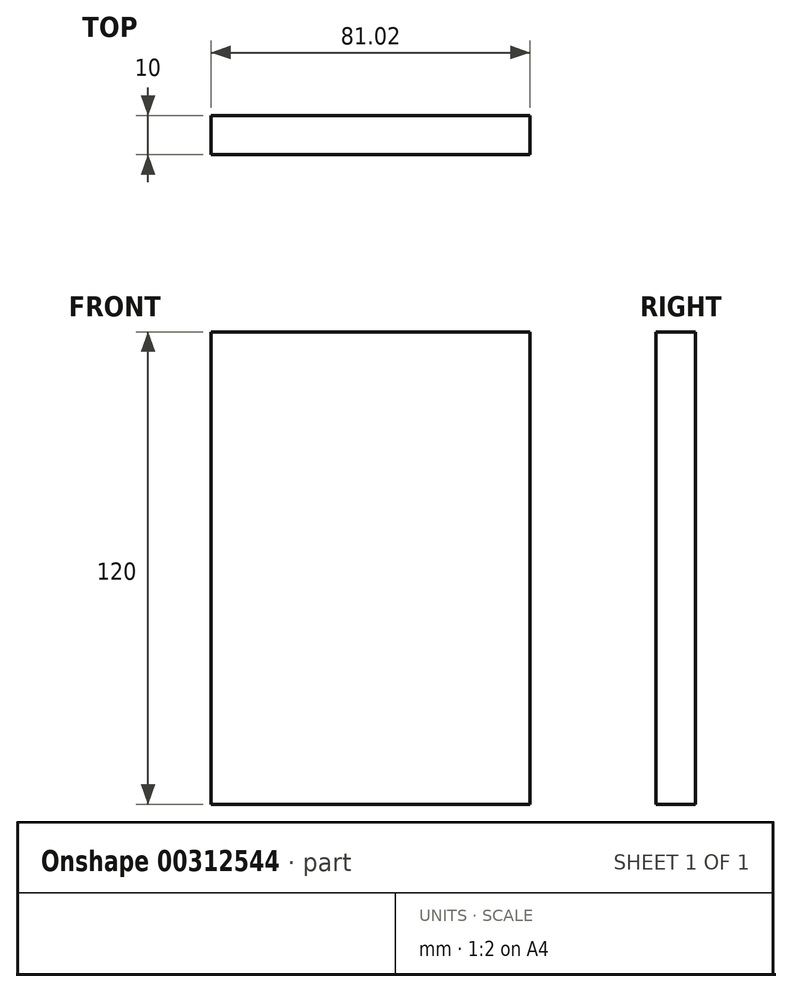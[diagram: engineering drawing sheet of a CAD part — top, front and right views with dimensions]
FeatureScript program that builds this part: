
annotation { "Feature Type Name" : "Feature", "Feature Type Description" : "" }
export const myFeature = defineFeature(function(context is Context, id is Id, definition is map)
    precondition{}
    {
        {
            var Q0;
            Q0=qCreatedBy(makeId("Front.planeOp"),FACE);
            var sketch = newSketch(context, id + "F0", { "sketchPlane" : qUnion([Q0])});
            skLineSegment(sketch, "E0.bottom", {"start": v(40.5, 60) * mm, "end": v(-40.51, 60) * mm});
            skLineSegment(sketch, "E0.top", {"start": v(40.51, -60) * mm, "end": v(-40.5, -60) * mm});
            skLineSegment(sketch, "E0.left", {"start": v(40.5, 60) * mm, "end": v(40.51, -60) * mm});
            skLineSegment(sketch, "E0.right", {"start": v(-40.51, 60) * mm, "end": v(-40.5, -60) * mm});
            skPoint(sketch, "E0.middle", {"position": v(0, 0) * mm});
            skSolve(sketch);
        }
        {
            var Q0;
            Q0=makeQuery(id+"F0.imprint","IMPRINT",FACE,{"disambiguationData":[TD([[makeQuery(id+"F0.imprint","IMPRINT",EDGE,{"derivedFrom":sQuery(id+"F0.wireOp",EDGE,"E0.bottom")}),1.0]])]});
            extrude(context, id + "F1", {"entities" : qUnion([Q0]), "depth" : 10 * mm});
        }
    });
